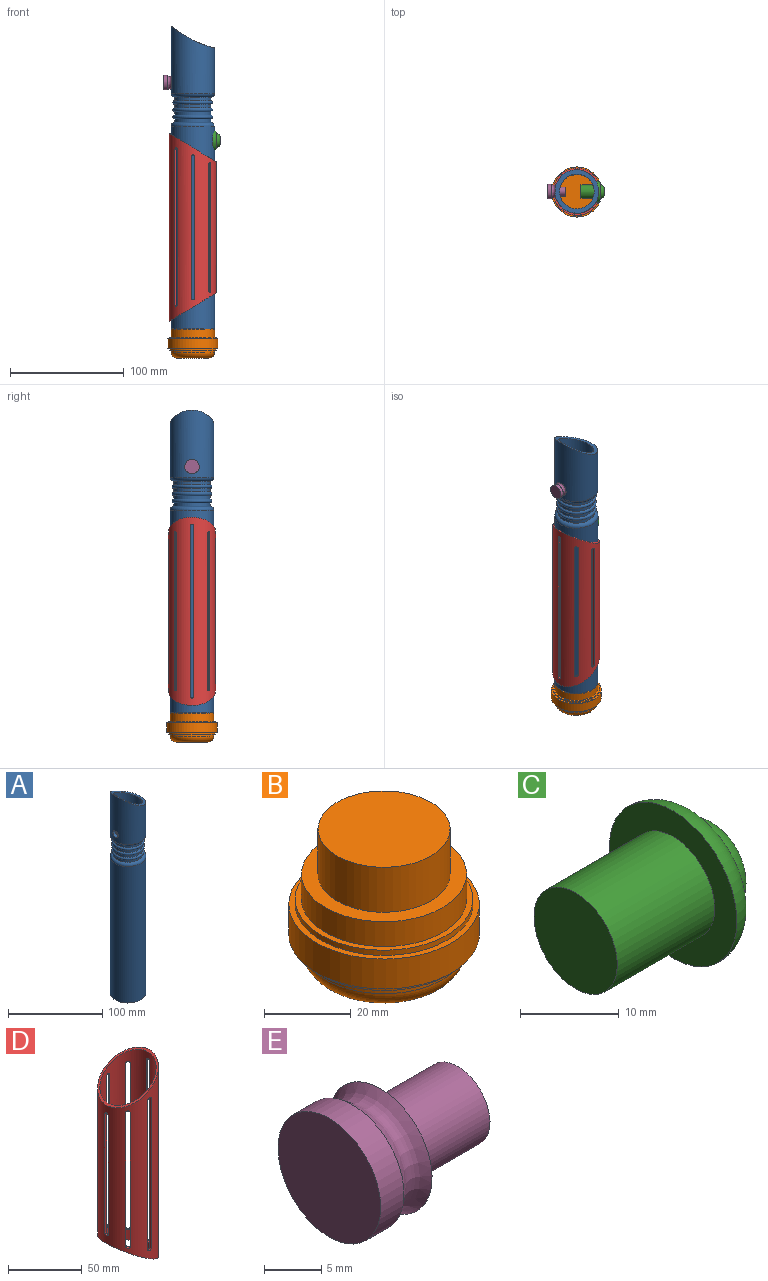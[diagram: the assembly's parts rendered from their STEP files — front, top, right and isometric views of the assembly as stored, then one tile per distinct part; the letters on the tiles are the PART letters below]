
ASSEMBLY  parts=5 mates=4
PART A: 16 faces, bbox 41.2x41.2x265.6 mm
  f0: cylinder r=19.05mm len=177.8mm, axis (0,0,-1), area 21168.3mm2, adj f3,f12,f14
  f1: cylinder r=15.24mm len=262.57mm, axis (0,0,-1), area 24160.8mm2, adj f3,f11,f14,f15
  f2: cylinder r=19.05mm len=59.23mm, axis (0,0,-1), area 5714.6mm2, adj f11,f13,f15
  f3: plane 38.1x38.1mm, normal (0,0,-1), area 410.4mm2, adj f0,f1
  f4: cylinder r=15.88mm len=31.75mm, axis (0,0,-1), area 316.7mm2, adj f5,f12
  f5: torus R=15.88mm, axis (0,0,-1), area 529.1mm2, adj f4,f6
  f6: cylinder r=15.88mm len=31.75mm, axis (0,0,-1), area 316.7mm2, adj f5,f7
  f7: torus R=15.88mm, axis (0,0,-1), area 529.1mm2, adj f6,f8
  f8: cylinder r=15.88mm len=31.75mm, axis (0,0,-1), area 316.7mm2, adj f7,f9
  f9: torus R=15.88mm, axis (0,0,-1), area 529.1mm2, adj f8,f10
  f10: cylinder r=15.88mm len=31.75mm, axis (0,0,-1), area 316.7mm2, adj f9,f13
  f11: cylinder r=94.59mm len=38.1mm, axis (0,-1,0), area 464.4mm2, adj f1,f2
  f12: torus R=15.88mm, axis (0,0,-1), area 560.8mm2, adj f0,f4
  f13: torus R=15.88mm, axis (0,0,1), area 560.8mm2, adj f2,f10
  f14: cylinder r=5.97mm len=11.94mm, axis (-1,0,0), area 147.7mm2, adj f0,f1
  f15: cylinder r=3.99mm len=7.98mm, axis (1,0,0), area 96.8mm2, adj f1,f2
PART B: 14 faces, bbox 44x44x38.1 mm
  f0: plane 38.1x38.1mm, normal (0,0,1), area 410.4mm2, adj f1,f12
  f1: cylinder r=15.24mm len=30.48mm, axis (0,0,1), area 1216.1mm2, adj f0,f2
  f2: plane 30.48x30.48mm, normal (0,0,1), area 729.7mm2, adj f1
  f3: plane 27.94x27.94mm, normal (0,0,-1), area 613.1mm2, adj f13
  f4: cylinder r=19.05mm len=38.1mm, axis (0,0,1), area 230.6mm2, adj f5,f13
  f5: plane 41.03x41.03mm, normal (0,0,-1), area 182mm2, adj f4,f6
  f6: cylinder r=20.51mm len=41.03mm, axis (0,0,1), area 188.7mm2, adj f5,f7
  f7: plane 43.96x43.96mm, normal (0,0,-1), area 195.5mm2, adj f6,f8
  f8: cylinder r=21.98mm len=43.96mm, axis (0,0,1), area 1168mm2, adj f7,f9
  f9: plane 43.96x43.96mm, normal (0,0,1), area 195.5mm2, adj f8,f10
  f10: cylinder r=20.51mm len=41.03mm, axis (0,0,1), area 188.7mm2, adj f9,f11
  f11: plane 41.03x41.03mm, normal (0,0,1), area 182mm2, adj f10,f12
  f12: cylinder r=19.05mm len=38.1mm, axis (0,0,1), area 838.7mm2, adj f0,f11
  f13: torus R=13.97mm, axis (0,0,1), area 862.6mm2, adj f3,f4
PART C: 6 faces, bbox 20.3x19.8x19.8 mm
  f0: plane 11.94x11.94mm, normal (-1,0,0), area 111.9mm2, adj f3
  f1: plane 5.59x5.59mm, normal (1,0,0), area 24.5mm2, adj f5
  f2: plane 18.29x18.29mm, normal (-1,0,0), area 150.7mm2, adj f3,f4
  f3: cylinder r=5.97mm len=13.97mm, axis (-1,0,0), area 523.9mm2, adj f0,f2
  f4: torus R=5.97mm, axis (-1,0,0), area 250.4mm2, adj f2,f5
  f5: torus R=2.79mm, axis (-1,0,0), area 150.9mm2, adj f1,f4
PART D: 37 faces, bbox 41.3x41.3x165.3 mm
  f0: cylinder r=20.64mm len=165.27mm, axis (0,0,-1), area 14936.1mm2, adj f2,f3,f4,f5,f6,f7,f8,f9
  f1: cylinder r=19.05mm len=163.43mm, axis (0,0,-1), area 13540.3mm2, adj f3,f4,f5,f6,f7,f8,f9,f10
  f2: plane 5.47x0.18mm, normal (0,0,-1), area 0.7mm2, adj f0,f3
  f3: plane 41.28x41.09mm, normal (-0.52,0,-0.85), area 231mm2, adj f0,f1,f2
  f4: plane 41.28x41.28mm, normal (-0.52,0,0.85), area 232.4mm2, adj f0,f1
  f5: plane 98.43x1.59mm, normal (0,-1,0), area 156.8mm2, adj f0,f1,f6,f8
  f6: cylinder r=1.59mm len=3.18mm, axis (1,0,0), area 7.9mm2, adj f0,f1,f5,f7
  f7: plane 98.43x1.59mm, normal (0,1,0), area 156.8mm2, adj f0,f1,f6,f8
  f8: cylinder r=1.59mm len=3.18mm, axis (1,0,0), area 7.9mm2, adj f0,f1,f5,f7
  f9: plane 149.23x1.59mm, normal (0,-1,0), area 237.7mm2, adj f0,f1,f10,f12
  f10: cylinder r=1.59mm len=3.18mm, axis (-1,0,0), area 7.9mm2, adj f0,f1,f9,f11
  f11: plane 149.23x1.59mm, normal (0,1,0), area 237.7mm2, adj f0,f1,f10,f12
  f12: cylinder r=1.59mm len=3.18mm, axis (-1,0,0), area 7.9mm2, adj f0,f1,f9,f11
  f13: cylinder r=1.59mm len=3.18mm, axis (0,1,0), area 7.9mm2, adj f0,f1,f14,f16
  f14: plane 123.83x1.59mm, normal (1,0,0), area 197.2mm2, adj f0,f1,f13,f15
  f15: cylinder r=1.59mm len=3.18mm, axis (0,1,0), area 7.9mm2, adj f0,f1,f14,f16
  f16: plane 123.83x1.59mm, normal (-1,0,0), area 197.2mm2, adj f0,f1,f13,f15
  f17: plane 123.83x1.59mm, normal (-1,0,0), area 197.2mm2, adj f0,f1,f18,f20
  f18: cylinder r=1.59mm len=3.18mm, axis (0,1,0), area 7.9mm2, adj f0,f1,f17,f19
  f19: plane 123.83x1.59mm, normal (1,0,0), area 197.2mm2, adj f0,f1,f18,f20
  f20: cylinder r=1.59mm len=3.18mm, axis (0,1,0), area 7.9mm2, adj f0,f1,f17,f19
  f21: plane 110.62x1.13mm, normal (0.71,-0.71,0), area 176.2mm2, adj f0,f1,f22,f24
  f22: cylinder r=1.59mm len=3.37mm, axis (0.71,0.71,0), area 7.9mm2, adj f0,f1,f21,f23
  f23: plane 110.62x1.13mm, normal (-0.71,0.71,0), area 176.2mm2, adj f0,f1,f22,f24
  f24: cylinder r=1.59mm len=3.37mm, axis (0.71,0.71,0), area 7.9mm2, adj f0,f1,f21,f23
  f25: plane 136.53x1.13mm, normal (0.71,-0.71,0), area 217.4mm2, adj f0,f1,f26,f28
  f26: cylinder r=1.59mm len=3.37mm, axis (-0.71,-0.71,0), area 7.9mm2, adj f0,f1,f25,f27
  f27: plane 136.53x1.13mm, normal (-0.71,0.71,0), area 217.4mm2, adj f0,f1,f26,f28
  f28: cylinder r=1.59mm len=3.37mm, axis (-0.71,-0.71,0), area 7.9mm2, adj f0,f1,f25,f27
  f29: plane 110.62x1.13mm, normal (0.71,0.71,0), area 176.2mm2, adj f0,f1,f30,f32
  f30: cylinder r=1.59mm len=3.37mm, axis (0.71,-0.71,0), area 7.9mm2, adj f0,f1,f29,f31
  f31: plane 110.62x1.13mm, normal (-0.71,-0.71,0), area 176.2mm2, adj f0,f1,f30,f32
  f32: cylinder r=1.59mm len=3.37mm, axis (0.71,-0.71,0), area 7.9mm2, adj f0,f1,f29,f31
  f33: plane 136.53x1.13mm, normal (0.71,0.71,0), area 217.4mm2, adj f0,f1,f34,f36
  f34: cylinder r=1.6mm len=3.38mm, axis (-0.71,0.71,0), area 8mm2, adj f0,f1,f33,f35
  f35: plane 136.53x1.13mm, normal (-0.71,-0.71,0), area 217.4mm2, adj f0,f1,f34,f36
  f36: cylinder r=1.6mm len=3.38mm, axis (-0.71,0.71,0), area 8mm2, adj f0,f1,f33,f35
PART E: 6 faces, bbox 15.9x12.7x12.7 mm
  f0: plane 12.7x12.7mm, normal (1,0,0), area 76.7mm2, adj f1,f5
  f1: cylinder r=3.99mm len=9.53mm, axis (1,0,0), area 238.7mm2, adj f0,f2
  f2: plane 7.98x7.98mm, normal (1,0,0), area 50mm2, adj f1
  f3: plane 12.7x12.7mm, normal (-1,0,0), area 126.7mm2, adj f4
  f4: cylinder r=6.35mm len=12.7mm, axis (1,0,0), area 114.8mm2, adj f3,f5
  f5: revolved ~12.7x12.7mm, area 148mm2, adj f0,f4
PLACE A rot(axis=(-0.01,-1,0),0deg) t=(53.99,-12.78,-17.57)mm
PLACE B t=(53.99,-12.78,-17.97)mm
PLACE C rot(axis=(-1,0,0),0deg) t=(57.57,-12.78,147.53)mm
PLACE D rot(axis=(0,0,1),180deg) t=(53.99,-12.78,-11.13)mm
PLACE E t=(44.46,-12.78,198.33)mm
MATE slider B.f1 <-> A.f1  axis (0,0,1) through (53.99,-12.78,-5.27)mm
MATE cylindrical D.f1 <-> A.f0  axis (0,0,-1) through (53.99,-12.78,153.97)mm
MATE cylindrical A.f15 <-> E.f1  axis (1,0,0) through (34.9,-12.78,198.33)mm
MATE cylindrical C.f3 <-> A.f14  axis (-1,0,0) through (57.57,-12.78,147.53)mm
